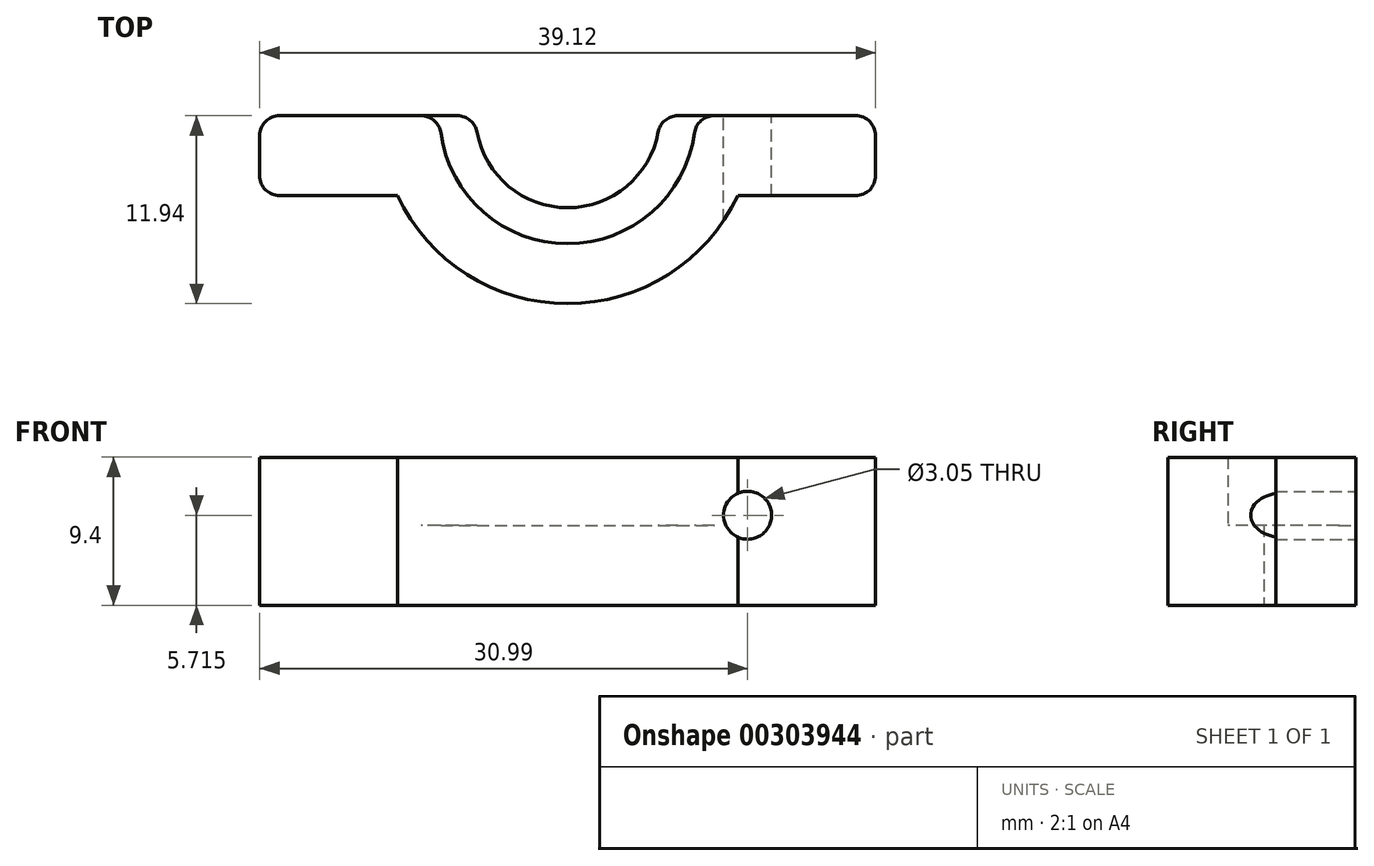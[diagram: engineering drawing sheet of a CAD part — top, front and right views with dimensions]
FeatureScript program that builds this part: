
annotation { "Feature Type Name" : "Feature", "Feature Type Description" : "" }
export const myFeature = defineFeature(function(context is Context, id is Id, definition is map)
    precondition{}
    {
        {
            var Q0;
            Q0=qCreatedBy(makeId("Top.planeOp"),FACE);
            var sketch = newSketch(context, id + "F0", { "sketchPlane" : qUnion([Q0])});
            skArc(sketch, "E0", {"start": v(-5.84, 0) * mm, "mid": v(0, -5.84) * mm, "end": v(5.84, 0) * mm});
            skLineSegment(sketch, "E1", {"start": v(-5.84, 0) * mm, "end": v(5.84, 0) * mm});
            skArc(sketch, "E2.0", {"start": v(-8.13, 0) * mm, "mid": v(0, -8.13) * mm, "end": v(8.13, 0) * mm});
            skLineSegment(sketch, "E3", {"start": v(-5.84, 0) * mm, "end": v(-8.13, 0) * mm});
            skLineSegment(sketch, "E4", {"start": v(5.84, 0) * mm, "end": v(8.13, 0) * mm});
            skArc(sketch, "E5.0", {"start": v(-11.94, 0) * mm, "mid": v(0, -11.94) * mm, "end": v(11.94, 0) * mm});
            skLineSegment(sketch, "E6", {"start": v(11.94, 0) * mm, "end": v(19.56, 0) * mm});
            skLineSegment(sketch, "E7", {"start": v(19.56, 0) * mm, "end": v(19.56, -5.08) * mm});
            skLineSegment(sketch, "E8", {"start": v(19.56, -5.08) * mm, "end": v(10.8, -5.08) * mm});
            skLineSegment(sketch, "E9.MirrorCS", {"start": v(19.56, 0) * mm, "end": v(19.56, 5.08) * mm});
            skLineSegment(sketch, "E10.MirrorCS", {"start": v(19.56, 5.08) * mm, "end": v(10.8, 5.08) * mm});
            skLineSegment(sketch, "E11", {"start": v(0, 0) * mm, "end": v(0, -11.94) * mm, "construction": true});
            skLineSegment(sketch, "E12.MirrorCS", {"start": v(-11.94, 0) * mm, "end": v(-19.56, 0) * mm});
            skLineSegment(sketch, "E13.MirrorCS", {"start": v(-19.56, 0) * mm, "end": v(-19.56, -5.08) * mm});
            skLineSegment(sketch, "E14.MirrorCS", {"start": v(-19.56, -5.08) * mm, "end": v(-10.8, -5.08) * mm});
            skLineSegment(sketch, "E15", {"start": v(-11.94, 0) * mm, "end": v(-8.13, 0) * mm});
            skLineSegment(sketch, "E16", {"start": v(8.13, 0) * mm, "end": v(11.94, 0) * mm});
            skSolve(sketch);
        }
        {
            var Q0;
            {var subQ0=sQuery(id+"F0.wireOp",EDGE,"E12.MirrorCS");Q0=makeQuery(id+"F0.imprint","IMPRINT",FACE,{"disambiguationData":[TD([[makeQuery(id+"F0.imprint","IMPRINT",EDGE,{"derivedFrom":subQ0}),1.0]])]});}
            var Q1;
            Q1=makeQuery(id+"F0.imprint","IMPRINT",FACE,{"disambiguationData":[TD([[makeQuery(id+"F0.imprint","IMPRINT",EDGE,{"derivedFrom":sQuery(id+"F0.wireOp",EDGE,"E2.0")}),-1.0]])]});
            var Q2;
            {var subQ0=sQuery(id+"F0.wireOp",EDGE,"E6");Q2=makeQuery(id+"F0.imprint","IMPRINT",FACE,{"disambiguationData":[TD([[makeQuery(id+"F0.imprint","IMPRINT",EDGE,{"derivedFrom":subQ0}),-1.0]])]});}
            extrude(context, id + "F1", {"entities" : qUnion([Q0, Q1, Q2]), "depth" : 9.4 * mm});
        }
        {
            var Q0;
            Q0=makeQuery(id+"F0.imprint","IMPRINT",FACE,{"disambiguationData":[TD([[makeQuery(id+"F0.imprint","IMPRINT",EDGE,{"derivedFrom":sQuery(id+"F0.wireOp",EDGE,"E0")}),-1.0]])]});
            extrude(context, id + "F2", {"entities" : qUnion([Q0]), "operationType" : NewBodyOperationType.ADD, "depth" : 5.08 * mm});
        }
        {
            var Q0;
            Q0=makeQuery(id+"F2.boolean.opBoolean","MERGE",FACE,{"derivedFrom":[makeQuery(id+"F1.opExtrude","SWEPT_FACE",FACE,{"disambiguationData":[OSD([sQuery(id+"F0.wireOp",EDGE,"E6"),sQuery(id+"F0.wireOp",EDGE,"E16")])]}),makeQuery(id+"F2.opExtrude","SWEPT_FACE",FACE,{"disambiguationData":[OSD([sQuery(id+"F0.wireOp",EDGE,"E4")])]})]});
            var sketch = newSketch(context, id + "F3", { "sketchPlane" : qUnion([Q0])});
            skLineSegment(sketch, "E17", {"start": v(-5.84, 5.72) * mm, "end": v(-19.56, 5.72) * mm, "construction": true});
            skLineSegment(sketch, "E18", {"start": v(-5.84, 5.72) * mm, "end": v(-11.43, 5.72) * mm, "construction": true});
            skLineSegment(sketch, "E19", {"start": v(-11.43, 5.72) * mm, "end": v(-11.43, 7.29) * mm, "construction": true});
            skCircle(sketch, "E20", {"center": v(-11.43, 5.72) * mm, "radius": 1.52 * mm});
            skCircle(sketch, "E21.MirrorC", {"center": v(11.43, 5.72) * mm, "radius": 1.52 * mm});
            skSolve(sketch);
        }
        {
            var Q0;
            Q0=makeQuery(id+"F3.imprint","IMPRINT",FACE,{"disambiguationData":[TD([[makeQuery(id+"F3.imprint","IMPRINT",EDGE,{"derivedFrom":sQuery(id+"F3.wireOp",EDGE,"E20")}),1.0]])]});
            var Q1;
            Q1=makeQuery(id+"F3.imprint","IMPRINT",FACE,{"disambiguationData":[TD([[makeQuery(id+"F3.imprint","IMPRINT",EDGE,{"derivedFrom":sQuery(id+"F3.wireOp",EDGE,"E21.MirrorC")}),-1.0]])]});
            extrude(context, id + "F4", {"entities" : qUnion([Q0, Q1]), "operationType" : NewBodyOperationType.REMOVE, "endBound" : BoundingType.UP_TO_NEXT, "oppositeDirection" : true, "depth" : 25.4 * mm});
        }
        {
            var Q0;
            Q0=makeQuery(id+"F2.opExtrude","SWEPT_EDGE",EDGE,{"disambiguationData":[OSD([sQuery(id+"F0.wireOp",EDGE,"E0"),sQuery(id+"F0.wireOp",EDGE,"E1"),sQuery(id+"F0.wireOp",EDGE,"E4")])]});
            var Q1;
            Q1=makeQuery(id+"F2.opExtrude","SWEPT_EDGE",EDGE,{"disambiguationData":[OSD([sQuery(id+"F0.wireOp",EDGE,"E0"),sQuery(id+"F0.wireOp",EDGE,"E1"),sQuery(id+"F0.wireOp",EDGE,"E3")])]});
            var Q2;
            Q2=makeQuery(id+"F1.opExtrude","SWEPT_EDGE",EDGE,{"disambiguationData":[OSD([sQuery(id+"F0.wireOp",EDGE,"E2.0"),sQuery(id+"F0.wireOp",EDGE,"E4"),sQuery(id+"F0.wireOp",EDGE,"E16")])]});
            var Q3;
            Q3=makeQuery(id+"F1.opExtrude","SWEPT_EDGE",EDGE,{"disambiguationData":[OSD([sQuery(id+"F0.wireOp",EDGE,"E2.0"),sQuery(id+"F0.wireOp",EDGE,"E3"),sQuery(id+"F0.wireOp",EDGE,"E15")])]});
            var Q4;
            Q4=makeQuery(id+"F1.opExtrude","SWEPT_EDGE",EDGE,{"disambiguationData":[OSD([sQuery(id+"F0.wireOp",EDGE,"E6"),sQuery(id+"F0.wireOp",EDGE,"E7")])]});
            var Q5;
            Q5=makeQuery(id+"F1.opExtrude","SWEPT_EDGE",EDGE,{"disambiguationData":[OSD([sQuery(id+"F0.wireOp",EDGE,"E7"),sQuery(id+"F0.wireOp",EDGE,"E8")])]});
            var Q6;
            Q6=makeQuery(id+"F1.opExtrude","SWEPT_EDGE",EDGE,{"disambiguationData":[OSD([sQuery(id+"F0.wireOp",EDGE,"E12.MirrorCS"),sQuery(id+"F0.wireOp",EDGE,"E13.MirrorCS")])]});
            var Q7;
            Q7=makeQuery(id+"F1.opExtrude","SWEPT_EDGE",EDGE,{"disambiguationData":[OSD([sQuery(id+"F0.wireOp",EDGE,"E13.MirrorCS"),sQuery(id+"F0.wireOp",EDGE,"E14.MirrorCS")])]});
            fillet(context, id + "F5", {"entities" : qUnion([Q0, Q1, Q2, Q3, Q4, Q5, Q6, Q7]), "radius" : 1.27 * mm, "tangentPropagation" : true, "allowEdgeOverflow" : false});
        }
    });
